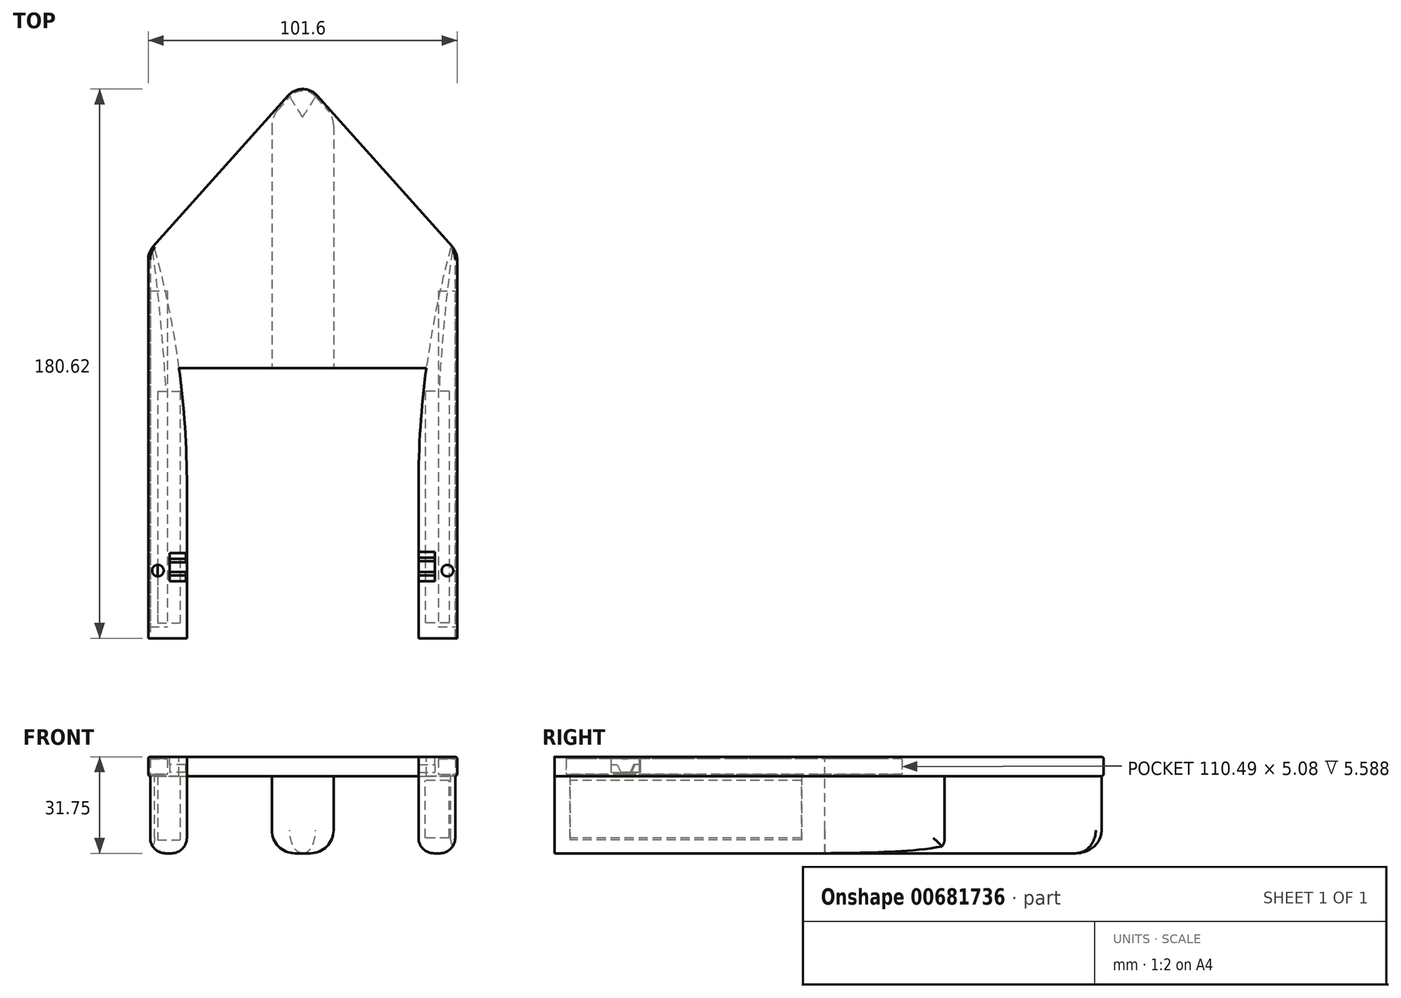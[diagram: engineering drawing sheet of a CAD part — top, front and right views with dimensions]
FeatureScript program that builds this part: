
annotation { "Feature Type Name" : "Feature", "Feature Type Description" : "" }
export const myFeature = defineFeature(function(context is Context, id is Id, definition is map)
    precondition{}
    {
        {
            var Q0;
            Q0=qCreatedBy(makeId("Top.planeOp"),FACE);
            var sketch = newSketch(context, id + "F0", { "sketchPlane" : qUnion([Q0])});
            skLineSegment(sketch, "E0", {"start": v(-75.35, 48.14) * mm, "end": v(-75.35, -78.86) * mm});
            skLineSegment(sketch, "E1", {"start": v(-75.35, -78.86) * mm, "end": v(26.25, -78.86) * mm});
            skLineSegment(sketch, "E2", {"start": v(26.25, -78.86) * mm, "end": v(26.25, 48.14) * mm});
            skLineSegment(sketch, "E3", {"start": v(-75.35, 48.14) * mm, "end": v(-24.55, 104.93) * mm});
            skLineSegment(sketch, "E4", {"start": v(-24.55, 104.93) * mm, "end": v(26.25, 48.14) * mm});
            skSolve(sketch);
        }
        {
            var Q0;
            Q0 = qSketchRegion(id + "F0", true);
            extrude(context, id + "F1", {"entities" : qUnion([Q0]), "depth" : 6.35 * mm, "offsetDistance" : 25.4 * mm});
        }
        {
            var Q0;
            Q0=makeQuery(id+"F1.opExtrude","SWEPT_EDGE",EDGE,{"disambiguationData":[OSD([sQuery(id+"F0.wireOp",EDGE,"E3"),sQuery(id+"F0.wireOp",EDGE,"E4")])]});
            var Q1;
            Q1=makeQuery(id+"F1.opExtrude","SWEPT_EDGE",EDGE,{"disambiguationData":[OSD([sQuery(id+"F0.wireOp",EDGE,"E0"),sQuery(id+"F0.wireOp",EDGE,"E3")])]});
            var Q2;
            Q2=makeQuery(id+"F1.opExtrude","SWEPT_EDGE",EDGE,{"disambiguationData":[OSD([sQuery(id+"F0.wireOp",EDGE,"E2"),sQuery(id+"F0.wireOp",EDGE,"E4")])]});
            fillet(context, id + "F2", {"entities" : qUnion([Q0, Q1, Q2]), "radius" : 6.35 * mm, "tangentPropagation" : true, "allowEdgeOverflow" : false});
        }
        {
            var Q0;
            Q0=makeQuery(id+"F1.opExtrude","CAP_EDGE",EDGE,{"disambiguationData":[OSD([sQuery(id+"F0.wireOp",EDGE,"E3")])],"isStart":false});
            var Q1;
            Q1=makeQuery(id+"F1.opExtrude","CAP_EDGE",EDGE,{"disambiguationData":[OSD([sQuery(id+"F0.wireOp",EDGE,"E4")])],"isStart":true});
            var Q2;
            Q2=makeQuery(id+"F1.opExtrude","CAP_EDGE",EDGE,{"disambiguationData":[OSD([sQuery(id+"F0.wireOp",EDGE,"E3")])],"isStart":true});
            var Q3;
            {var subQ0=sQuery(id+"F0.wireOp",EDGE,"E4");var subQ1=sQuery(id+"F0.wireOp",EDGE,"E3");Q3=makeQuery(id+"F2.opFillet","BLEND_EDGE",EDGE,{"blendedFrom":[makeQuery(id+"F1.opExtrude","SWEPT_EDGE",EDGE,{"disambiguationData":[OSD([subQ1,subQ0])]}),makeQuery(id+"F1.opExtrude","CAP_FACE",FACE,{"disambiguationData":[OSD([sQuery(id+"F0.wireOp",EDGE,"E0"),sQuery(id+"F0.wireOp",EDGE,"E1"),sQuery(id+"F0.wireOp",EDGE,"E2"),subQ1,subQ0])],"isStart":true})],"blendedInto":[makeQuery(id+"F1.opExtrude","CAP_FACE",FACE,{"disambiguationData":[OSD([sQuery(id+"F0.wireOp",EDGE,"E0"),sQuery(id+"F0.wireOp",EDGE,"E1"),sQuery(id+"F0.wireOp",EDGE,"E2"),subQ1,subQ0])],"isStart":true})]});}
            fillet(context, id + "F3", {"entities" : qUnion([Q0, Q1, Q2, Q3]), "radius" : 0.64 * mm, "tangentPropagation" : true, "allowEdgeOverflow" : false});
        }
        {
            var Q0;
            Q0=makeQuery(id+"F1.opExtrude","CAP_FACE",FACE,{"disambiguationData":[OSD([sQuery(id+"F0.wireOp",EDGE,"E0"),sQuery(id+"F0.wireOp",EDGE,"E1"),sQuery(id+"F0.wireOp",EDGE,"E2"),sQuery(id+"F0.wireOp",EDGE,"E3"),sQuery(id+"F0.wireOp",EDGE,"E4")])],"isStart":false});
            var sketch = newSketch(context, id + "F4", { "sketchPlane" : qUnion([Q0])});
            skLineSegment(sketch, "E5.bottom", {"start": v(-62.65, -78.86) * mm, "end": v(13.55, -78.86) * mm});
            skLineSegment(sketch, "E5.top", {"start": v(-62.65, 10.04) * mm, "end": v(13.55, 10.04) * mm});
            skLineSegment(sketch, "E5.left", {"start": v(-62.65, -78.86) * mm, "end": v(-62.65, 10.04) * mm});
            skLineSegment(sketch, "E5.right", {"start": v(13.55, -78.86) * mm, "end": v(13.55, 10.04) * mm});
            skSolve(sketch);
        }
        {
            var Q0;
            Q0 = qSketchRegion(id + "F4", true);
            extrude(context, id + "F5", {"entities" : qUnion([Q0]), "operationType" : NewBodyOperationType.REMOVE, "oppositeDirection" : true, "depth" : 25.4 * mm, "offsetDistance" : 25.4 * mm});
        }
        {
            var Q0;
            Q0=makeQuery(id+"F1.opExtrude","CAP_FACE",FACE,{"disambiguationData":[OSD([sQuery(id+"F0.wireOp",EDGE,"E0"),sQuery(id+"F0.wireOp",EDGE,"E1"),sQuery(id+"F0.wireOp",EDGE,"E2"),sQuery(id+"F0.wireOp",EDGE,"E3"),sQuery(id+"F0.wireOp",EDGE,"E4")])],"isStart":false});
            var sketch = newSketch(context, id + "F6", { "sketchPlane" : qUnion([Q0])});
            skLineSegment(sketch, "E6.bottom", {"start": v(-62.65, -60.09) * mm, "end": v(-68.37, -60.09) * mm});
            skLineSegment(sketch, "E6.top", {"start": v(-62.65, -50.86) * mm, "end": v(-68.37, -50.86) * mm});
            skLineSegment(sketch, "E6.left", {"start": v(-62.65, -60.09) * mm, "end": v(-62.65, -50.86) * mm});
            skLineSegment(sketch, "E6.right", {"start": v(-68.37, -60.09) * mm, "end": v(-68.37, -50.86) * mm});
            skSolve(sketch);
        }
        {
            var Q0;
            Q0 = qSketchRegion(id + "F6", true);
            extrude(context, id + "F7", {"entities" : qUnion([Q0]), "operationType" : NewBodyOperationType.REMOVE, "oppositeDirection" : true, "depth" : 5.08 * mm, "offsetDistance" : 25.4 * mm});
        }
        {
            var Q0;
            Q0=makeQuery(id+"F1.opExtrude","CAP_FACE",FACE,{"disambiguationData":[OSD([sQuery(id+"F0.wireOp",EDGE,"E0"),sQuery(id+"F0.wireOp",EDGE,"E1"),sQuery(id+"F0.wireOp",EDGE,"E2"),sQuery(id+"F0.wireOp",EDGE,"E3"),sQuery(id+"F0.wireOp",EDGE,"E4")])],"isStart":false});
            var sketch = newSketch(context, id + "F8", { "sketchPlane" : qUnion([Q0])});
            skLineSegment(sketch, "E7.bottom", {"start": v(13.55, -50.5) * mm, "end": v(18.92, -50.5) * mm});
            skLineSegment(sketch, "E7.top", {"start": v(13.55, -60.09) * mm, "end": v(18.92, -60.09) * mm});
            skLineSegment(sketch, "E7.left", {"start": v(13.55, -50.5) * mm, "end": v(13.55, -60.09) * mm});
            skLineSegment(sketch, "E7.right", {"start": v(18.92, -50.5) * mm, "end": v(18.92, -60.09) * mm});
            skSolve(sketch);
        }
        {
            var Q0;
            Q0 = qSketchRegion(id + "F8", true);
            extrude(context, id + "F9", {"entities" : qUnion([Q0]), "operationType" : NewBodyOperationType.REMOVE, "oppositeDirection" : true, "depth" : 5.08 * mm, "offsetDistance" : 25.4 * mm});
        }
        {
            var Q0;
            Q0=makeQuery(id+"F7.boolean.opBoolean","COPY",FACE,{"derivedFrom":makeQuery(id+"F7.opExtrude","SWEPT_FACE",FACE,{"disambiguationData":[OSD([sQuery(id+"F6.wireOp",EDGE,"E6.right")])]})});
            var sketch = newSketch(context, id + "F10", { "sketchPlane" : qUnion([Q0])});
            skLineSegment(sketch, "E8", {"start": v(-60.09, 3.81) * mm, "end": v(-58.18, 3.81) * mm});
            skLineSegment(sketch, "E9", {"start": v(-58.18, 3.81) * mm, "end": v(-57.02, 1.27) * mm});
            skLineSegment(sketch, "E10", {"start": v(-57.02, 1.27) * mm, "end": v(-60.09, 1.27) * mm});
            skLineSegment(sketch, "E11", {"start": v(-60.09, 1.27) * mm, "end": v(-60.09, 3.81) * mm});
            skLineSegment(sketch, "E12", {"start": v(-50.86, 3.81) * mm, "end": v(-52.76, 3.81) * mm});
            skLineSegment(sketch, "E13", {"start": v(-52.76, 3.8) * mm, "end": v(-53.93, 1.27) * mm});
            skLineSegment(sketch, "E14", {"start": v(-53.93, 1.27) * mm, "end": v(-50.86, 1.27) * mm});
            skLineSegment(sketch, "E15", {"start": v(-50.86, 1.27) * mm, "end": v(-50.86, 3.81) * mm});
            skSolve(sketch);
        }
        {
            var Q0;
            Q0=makeQuery(id+"F9.boolean.opBoolean","COPY",FACE,{"derivedFrom":makeQuery(id+"F9.opExtrude","SWEPT_FACE",FACE,{"disambiguationData":[OSD([sQuery(id+"F8.wireOp",EDGE,"E7.right")])]})});
            var sketch = newSketch(context, id + "F11", { "sketchPlane" : qUnion([Q0])});
            skLineSegment(sketch, "E16", {"start": v(50.5, 3.81) * mm, "end": v(52.4, 3.81) * mm});
            skLineSegment(sketch, "E17", {"start": v(52.4, 3.81) * mm, "end": v(53.56, 1.27) * mm});
            skLineSegment(sketch, "E18", {"start": v(53.56, 1.27) * mm, "end": v(50.5, 1.27) * mm});
            skLineSegment(sketch, "E19", {"start": v(50.5, 1.27) * mm, "end": v(50.5, 3.81) * mm});
            skLineSegment(sketch, "E20", {"start": v(60.09, 3.81) * mm, "end": v(58.18, 3.81) * mm});
            skLineSegment(sketch, "E21", {"start": v(58.18, 3.81) * mm, "end": v(57.02, 1.27) * mm});
            skLineSegment(sketch, "E22", {"start": v(57.02, 1.27) * mm, "end": v(60.09, 1.27) * mm});
            skLineSegment(sketch, "E23", {"start": v(60.09, 1.27) * mm, "end": v(60.09, 3.81) * mm});
            skSolve(sketch);
        }
        {
            var Q0;
            Q0 = qSketchRegion(id + "F10", true);
            extrude(context, id + "F12", {"entities" : qUnion([Q0]), "operationType" : NewBodyOperationType.ADD, "depth" : 5.33 * mm, "offsetDistance" : 25.4 * mm});
        }
        {
            var Q0;
            Q0 = qSketchRegion(id + "F11", true);
            extrude(context, id + "F13", {"entities" : qUnion([Q0]), "operationType" : NewBodyOperationType.ADD, "depth" : 5.33 * mm, "offsetDistance" : 25.4 * mm});
        }
        {
            var Q0;
            {var subQ0=sQuery(id+"FkVk3INAum2beZh_1.wireOp",EDGE,"CBnXaj17-lKBn-qkcq-8vhT-qGtuAPUyLBLH.right");var subQ1=sQuery(id+"FkVk3INAum2beZh_1.wireOp",EDGE,"CBnXaj17-lKBn-qkcq-8vhT-qGtuAPUyLBLH.top");var subQ2=sQuery(id+"FkVk3INAum2beZh_1.wireOp",EDGE,"CBnXaj17-lKBn-qkcq-8vhT-qGtuAPUyLBLH.left");var subQ3=sQuery(id+"F0.wireOp",EDGE,"E0");var subQ7=sQuery(id+"F0.wireOp",EDGE,"E1");Q0=makeQuery(id+"F5p0aCiFBfXdLHS_1.boolean.opBoolean","MERGE",FACE,{"derivedFrom":[makeQuery(id+"F5.boolean.opBoolean","SPLIT",FACE,{"disambiguationData":[TD([makeQuery(id+"F1.opExtrude","SWEPT_FACE",FACE,{"disambiguationData":[OSD([subQ3])]})])],"derivedFrom":makeQuery(id+"FswQXXDHsv7HpHE_1.boolean.opBoolean","MERGE",FACE,{"derivedFrom":[makeQuery(id+"F1.opExtrude","SWEPT_FACE",FACE,{"disambiguationData":[OSD([subQ7])]}),makeQuery(id+"FswQXXDHsv7HpHE_1.opExtrude","CAP_FACE",FACE,{"disambiguationData":[OSD([sQuery(id+"FkVk3INAum2beZh_1.wireOp",EDGE,"CBnXaj17-lKBn-qkcq-8vhT-qGtuAPUyLBLH.bottom"),subQ1,subQ2,subQ0])],"isStart":true}),makeQuery(id+"FswQXXDHsv7HpHE_1.opExtrude","CAP_FACE",FACE,{"disambiguationData":[OSD([sQuery(id+"FkVk3INAum2beZh_1.wireOp",EDGE,"G5rZIyKY-4YGs-gmH6-VOyw-JunLJIaNOIT2.bottom"),sQuery(id+"FkVk3INAum2beZh_1.wireOp",EDGE,"G5rZIyKY-4YGs-gmH6-VOyw-JunLJIaNOIT2.top"),sQuery(id+"FkVk3INAum2beZh_1.wireOp",EDGE,"G5rZIyKY-4YGs-gmH6-VOyw-JunLJIaNOIT2.left"),sQuery(id+"FkVk3INAum2beZh_1.wireOp",EDGE,"G5rZIyKY-4YGs-gmH6-VOyw-JunLJIaNOIT2.right")])],"isStart":true})]})}),makeQuery(id+"F5p0aCiFBfXdLHS_1.opExtrude","CAP_FACE",FACE,{"disambiguationData":[OSD([sQuery(id+"FsEtyhvZ73HZmaM_1.wireOp",EDGE,"eh50Zago-m3CJ-1YUL-9TTU-CO1hKXEADzyN.bottom"),sQuery(id+"FsEtyhvZ73HZmaM_1.wireOp",EDGE,"eh50Zago-m3CJ-1YUL-9TTU-CO1hKXEADzyN.top"),sQuery(id+"FsEtyhvZ73HZmaM_1.wireOp",EDGE,"eh50Zago-m3CJ-1YUL-9TTU-CO1hKXEADzyN.left"),sQuery(id+"FsEtyhvZ73HZmaM_1.wireOp",EDGE,"eh50Zago-m3CJ-1YUL-9TTU-CO1hKXEADzyN.right")])],"isStart":true})]});}
            var sketch = newSketch(context, id + "F14", { "sketchPlane" : qUnion([Q0])});
            skLineSegment(sketch, "E24.bottom", {"start": v(-74.72, 5.72) * mm, "end": v(-69.13, 5.72) * mm});
            skLineSegment(sketch, "E24.top", {"start": v(-74.72, 0.63) * mm, "end": v(-69.13, 0.63) * mm});
            skLineSegment(sketch, "E24.left", {"start": v(-74.72, 5.72) * mm, "end": v(-74.72, 0.63) * mm});
            skLineSegment(sketch, "E24.right", {"start": v(-69.13, 5.72) * mm, "end": v(-69.13, 0.63) * mm});
            skSolve(sketch);
        }
        {
            var Q0;
            {var subQ0=sQuery(id+"FkVk3INAum2beZh_1.wireOp",EDGE,"G5rZIyKY-4YGs-gmH6-VOyw-JunLJIaNOIT2.right");var subQ1=sQuery(id+"FkVk3INAum2beZh_1.wireOp",EDGE,"G5rZIyKY-4YGs-gmH6-VOyw-JunLJIaNOIT2.top");var subQ2=sQuery(id+"F0.wireOp",EDGE,"E2");var subQ3=sQuery(id+"FkVk3INAum2beZh_1.wireOp",EDGE,"G5rZIyKY-4YGs-gmH6-VOyw-JunLJIaNOIT2.left");var subQ6=sQuery(id+"F0.wireOp",EDGE,"E1");Q0=makeQuery(id+"FzT6SfWKQMYkcEQ_1.boolean.opBoolean","MERGE",FACE,{"derivedFrom":[makeQuery(id+"F5.boolean.opBoolean","SPLIT",FACE,{"disambiguationData":[TD([makeQuery(id+"F1.opExtrude","SWEPT_FACE",FACE,{"disambiguationData":[OSD([subQ2])]})])],"derivedFrom":makeQuery(id+"FswQXXDHsv7HpHE_1.boolean.opBoolean","MERGE",FACE,{"derivedFrom":[makeQuery(id+"F1.opExtrude","SWEPT_FACE",FACE,{"disambiguationData":[OSD([subQ6])]}),makeQuery(id+"FswQXXDHsv7HpHE_1.opExtrude","CAP_FACE",FACE,{"disambiguationData":[OSD([sQuery(id+"FkVk3INAum2beZh_1.wireOp",EDGE,"CBnXaj17-lKBn-qkcq-8vhT-qGtuAPUyLBLH.bottom"),sQuery(id+"FkVk3INAum2beZh_1.wireOp",EDGE,"CBnXaj17-lKBn-qkcq-8vhT-qGtuAPUyLBLH.top"),sQuery(id+"FkVk3INAum2beZh_1.wireOp",EDGE,"CBnXaj17-lKBn-qkcq-8vhT-qGtuAPUyLBLH.left"),sQuery(id+"FkVk3INAum2beZh_1.wireOp",EDGE,"CBnXaj17-lKBn-qkcq-8vhT-qGtuAPUyLBLH.right")])],"isStart":true}),makeQuery(id+"FswQXXDHsv7HpHE_1.opExtrude","CAP_FACE",FACE,{"disambiguationData":[OSD([sQuery(id+"FkVk3INAum2beZh_1.wireOp",EDGE,"G5rZIyKY-4YGs-gmH6-VOyw-JunLJIaNOIT2.bottom"),subQ1,subQ3,subQ0])],"isStart":true})]})}),makeQuery(id+"FzT6SfWKQMYkcEQ_1.opExtrude","CAP_FACE",FACE,{"disambiguationData":[OSD([sQuery(id+"F95VfNdrVZvIhjE_1.wireOp",EDGE,"nyIf93XB-J9r0-geGF-N8j9-ZKfysJtzp2Ce.bottom"),sQuery(id+"F95VfNdrVZvIhjE_1.wireOp",EDGE,"nyIf93XB-J9r0-geGF-N8j9-ZKfysJtzp2Ce.top"),sQuery(id+"F95VfNdrVZvIhjE_1.wireOp",EDGE,"nyIf93XB-J9r0-geGF-N8j9-ZKfysJtzp2Ce.left"),sQuery(id+"F95VfNdrVZvIhjE_1.wireOp",EDGE,"nyIf93XB-J9r0-geGF-N8j9-ZKfysJtzp2Ce.right")])],"isStart":true})]});}
            var sketch = newSketch(context, id + "F15", { "sketchPlane" : qUnion([Q0])});
            skLineSegment(sketch, "E25.bottom", {"start": v(20.02, 5.72) * mm, "end": v(25.61, 5.72) * mm});
            skLineSegment(sketch, "E25.top", {"start": v(20.02, 0.64) * mm, "end": v(25.61, 0.64) * mm});
            skLineSegment(sketch, "E25.left", {"start": v(20.02, 5.72) * mm, "end": v(20.02, 0.64) * mm});
            skLineSegment(sketch, "E25.right", {"start": v(25.61, 5.72) * mm, "end": v(25.61, 0.64) * mm});
            skSolve(sketch);
        }
        {
            var Q0;
            Q0 = qSketchRegion(id + "F14", true);
            extrude(context, id + "F16", {"entities" : qUnion([Q0]), "operationType" : NewBodyOperationType.REMOVE, "oppositeDirection" : true, "depth" : 114.3 * mm, "offsetDistance" : 25.4 * mm});
        }
        {
            var Q0;
            Q0 = qSketchRegion(id + "F15", true);
            extrude(context, id + "F17", {"entities" : qUnion([Q0]), "operationType" : NewBodyOperationType.REMOVE, "oppositeDirection" : true, "depth" : 114.3 * mm, "offsetDistance" : 25.4 * mm});
        }
        {
            var Q0;
            {var subQ0=sQuery(id+"FkVk3INAum2beZh_1.wireOp",EDGE,"G5rZIyKY-4YGs-gmH6-VOyw-JunLJIaNOIT2.right");var subQ1=sQuery(id+"FkVk3INAum2beZh_1.wireOp",EDGE,"G5rZIyKY-4YGs-gmH6-VOyw-JunLJIaNOIT2.top");var subQ2=sQuery(id+"F0.wireOp",EDGE,"E2");var subQ3=sQuery(id+"FkVk3INAum2beZh_1.wireOp",EDGE,"G5rZIyKY-4YGs-gmH6-VOyw-JunLJIaNOIT2.left");var subQ6=sQuery(id+"F0.wireOp",EDGE,"E1");Q0=makeQuery(id+"FzT6SfWKQMYkcEQ_1.boolean.opBoolean","MERGE",FACE,{"derivedFrom":[makeQuery(id+"F5.boolean.opBoolean","SPLIT",FACE,{"disambiguationData":[TD([makeQuery(id+"F1.opExtrude","SWEPT_FACE",FACE,{"disambiguationData":[OSD([subQ2])]})])],"derivedFrom":makeQuery(id+"FswQXXDHsv7HpHE_1.boolean.opBoolean","MERGE",FACE,{"derivedFrom":[makeQuery(id+"F1.opExtrude","SWEPT_FACE",FACE,{"disambiguationData":[OSD([subQ6])]}),makeQuery(id+"FswQXXDHsv7HpHE_1.opExtrude","CAP_FACE",FACE,{"disambiguationData":[OSD([sQuery(id+"FkVk3INAum2beZh_1.wireOp",EDGE,"CBnXaj17-lKBn-qkcq-8vhT-qGtuAPUyLBLH.bottom"),sQuery(id+"FkVk3INAum2beZh_1.wireOp",EDGE,"CBnXaj17-lKBn-qkcq-8vhT-qGtuAPUyLBLH.top"),sQuery(id+"FkVk3INAum2beZh_1.wireOp",EDGE,"CBnXaj17-lKBn-qkcq-8vhT-qGtuAPUyLBLH.left"),sQuery(id+"FkVk3INAum2beZh_1.wireOp",EDGE,"CBnXaj17-lKBn-qkcq-8vhT-qGtuAPUyLBLH.right")])],"isStart":true}),makeQuery(id+"FswQXXDHsv7HpHE_1.opExtrude","CAP_FACE",FACE,{"disambiguationData":[OSD([sQuery(id+"FkVk3INAum2beZh_1.wireOp",EDGE,"G5rZIyKY-4YGs-gmH6-VOyw-JunLJIaNOIT2.bottom"),subQ1,subQ3,subQ0])],"isStart":true})]})}),makeQuery(id+"FzT6SfWKQMYkcEQ_1.opExtrude","CAP_FACE",FACE,{"disambiguationData":[OSD([sQuery(id+"F95VfNdrVZvIhjE_1.wireOp",EDGE,"nyIf93XB-J9r0-geGF-N8j9-ZKfysJtzp2Ce.bottom"),sQuery(id+"F95VfNdrVZvIhjE_1.wireOp",EDGE,"nyIf93XB-J9r0-geGF-N8j9-ZKfysJtzp2Ce.top"),sQuery(id+"F95VfNdrVZvIhjE_1.wireOp",EDGE,"nyIf93XB-J9r0-geGF-N8j9-ZKfysJtzp2Ce.left"),sQuery(id+"F95VfNdrVZvIhjE_1.wireOp",EDGE,"nyIf93XB-J9r0-geGF-N8j9-ZKfysJtzp2Ce.right")])],"isStart":true})]});}
            var sketch = newSketch(context, id + "F18", { "sketchPlane" : qUnion([Q0])});
            skLineSegment(sketch, "E26.bottom", {"start": v(20.02, 5.72) * mm, "end": v(25.61, 5.72) * mm});
            skLineSegment(sketch, "E26.top", {"start": v(20.02, 0.64) * mm, "end": v(25.61, 0.64) * mm});
            skLineSegment(sketch, "E26.left", {"start": v(20.02, 5.72) * mm, "end": v(20.02, 0.64) * mm});
            skLineSegment(sketch, "E26.right", {"start": v(25.61, 5.72) * mm, "end": v(25.61, 0.64) * mm});
            skSolve(sketch);
        }
        {
            var Q0;
            Q0 = qSketchRegion(id + "F18", true);
            extrude(context, id + "F19", {"entities" : qUnion([Q0]), "operationType" : NewBodyOperationType.ADD, "oppositeDirection" : true, "depth" : 3.8 * mm, "offsetDistance" : 25.4 * mm});
        }
        {
            var Q0;
            {var subQ0=sQuery(id+"FkVk3INAum2beZh_1.wireOp",EDGE,"CBnXaj17-lKBn-qkcq-8vhT-qGtuAPUyLBLH.right");var subQ1=sQuery(id+"FkVk3INAum2beZh_1.wireOp",EDGE,"CBnXaj17-lKBn-qkcq-8vhT-qGtuAPUyLBLH.top");var subQ2=sQuery(id+"FkVk3INAum2beZh_1.wireOp",EDGE,"CBnXaj17-lKBn-qkcq-8vhT-qGtuAPUyLBLH.left");var subQ3=sQuery(id+"F0.wireOp",EDGE,"E0");var subQ7=sQuery(id+"F0.wireOp",EDGE,"E1");Q0=makeQuery(id+"F5p0aCiFBfXdLHS_1.boolean.opBoolean","MERGE",FACE,{"derivedFrom":[makeQuery(id+"F5.boolean.opBoolean","SPLIT",FACE,{"disambiguationData":[TD([makeQuery(id+"F1.opExtrude","SWEPT_FACE",FACE,{"disambiguationData":[OSD([subQ3])]})])],"derivedFrom":makeQuery(id+"FswQXXDHsv7HpHE_1.boolean.opBoolean","MERGE",FACE,{"derivedFrom":[makeQuery(id+"F1.opExtrude","SWEPT_FACE",FACE,{"disambiguationData":[OSD([subQ7])]}),makeQuery(id+"FswQXXDHsv7HpHE_1.opExtrude","CAP_FACE",FACE,{"disambiguationData":[OSD([sQuery(id+"FkVk3INAum2beZh_1.wireOp",EDGE,"CBnXaj17-lKBn-qkcq-8vhT-qGtuAPUyLBLH.bottom"),subQ1,subQ2,subQ0])],"isStart":true}),makeQuery(id+"FswQXXDHsv7HpHE_1.opExtrude","CAP_FACE",FACE,{"disambiguationData":[OSD([sQuery(id+"FkVk3INAum2beZh_1.wireOp",EDGE,"G5rZIyKY-4YGs-gmH6-VOyw-JunLJIaNOIT2.bottom"),sQuery(id+"FkVk3INAum2beZh_1.wireOp",EDGE,"G5rZIyKY-4YGs-gmH6-VOyw-JunLJIaNOIT2.top"),sQuery(id+"FkVk3INAum2beZh_1.wireOp",EDGE,"G5rZIyKY-4YGs-gmH6-VOyw-JunLJIaNOIT2.left"),sQuery(id+"FkVk3INAum2beZh_1.wireOp",EDGE,"G5rZIyKY-4YGs-gmH6-VOyw-JunLJIaNOIT2.right")])],"isStart":true})]})}),makeQuery(id+"F5p0aCiFBfXdLHS_1.opExtrude","CAP_FACE",FACE,{"disambiguationData":[OSD([sQuery(id+"FsEtyhvZ73HZmaM_1.wireOp",EDGE,"eh50Zago-m3CJ-1YUL-9TTU-CO1hKXEADzyN.bottom"),sQuery(id+"FsEtyhvZ73HZmaM_1.wireOp",EDGE,"eh50Zago-m3CJ-1YUL-9TTU-CO1hKXEADzyN.top"),sQuery(id+"FsEtyhvZ73HZmaM_1.wireOp",EDGE,"eh50Zago-m3CJ-1YUL-9TTU-CO1hKXEADzyN.left"),sQuery(id+"FsEtyhvZ73HZmaM_1.wireOp",EDGE,"eh50Zago-m3CJ-1YUL-9TTU-CO1hKXEADzyN.right")])],"isStart":true})]});}
            var sketch = newSketch(context, id + "F20", { "sketchPlane" : qUnion([Q0])});
            skLineSegment(sketch, "E27.bottom", {"start": v(-74.72, 5.72) * mm, "end": v(-69.13, 5.72) * mm});
            skLineSegment(sketch, "E27.top", {"start": v(-74.72, 0.63) * mm, "end": v(-69.13, 0.63) * mm});
            skLineSegment(sketch, "E27.left", {"start": v(-74.72, 5.72) * mm, "end": v(-74.72, 0.63) * mm});
            skLineSegment(sketch, "E27.right", {"start": v(-69.13, 5.72) * mm, "end": v(-69.13, 0.63) * mm});
            skSolve(sketch);
        }
        {
            var Q0;
            Q0 = qSketchRegion(id + "F20", true);
            extrude(context, id + "F21", {"entities" : qUnion([Q0]), "operationType" : NewBodyOperationType.ADD, "oppositeDirection" : true, "depth" : 3.8 * mm, "offsetDistance" : 25.4 * mm});
        }
        {
            var Q0;
            Q0=makeQuery(id+"F1.opExtrude","CAP_FACE",FACE,{"disambiguationData":[OSD([sQuery(id+"F0.wireOp",EDGE,"E0"),sQuery(id+"F0.wireOp",EDGE,"E1"),sQuery(id+"F0.wireOp",EDGE,"E2"),sQuery(id+"F0.wireOp",EDGE,"E3"),sQuery(id+"F0.wireOp",EDGE,"E4")])],"isStart":false});
            var sketch = newSketch(context, id + "F22", { "sketchPlane" : qUnion([Q0])});
            skCircle(sketch, "E28", {"center": v(-72.18, -56.64) * mm, "radius": 1.9 * mm});
            skCircle(sketch, "E29", {"center": v(23.07, -56.64) * mm, "radius": 1.9 * mm});
            skSolve(sketch);
        }
        {
            var Q0;
            Q0 = qSketchRegion(id + "F22", true);
            extrude(context, id + "F23", {"entities" : qUnion([Q0]), "operationType" : NewBodyOperationType.REMOVE, "oppositeDirection" : true, "depth" : 12.7 * mm, "offsetDistance" : 25.4 * mm});
        }
        {
            var Q0;
            Q0=makeQuery(id+"F1.opExtrude","CAP_FACE",FACE,{"disambiguationData":[OSD([sQuery(id+"F0.wireOp",EDGE,"E0"),sQuery(id+"F0.wireOp",EDGE,"E1"),sQuery(id+"F0.wireOp",EDGE,"E2"),sQuery(id+"F0.wireOp",EDGE,"E3"),sQuery(id+"F0.wireOp",EDGE,"E4")])],"isStart":true});
            var sketch = newSketch(context, id + "F24", { "sketchPlane" : qUnion([Q0])});
            skLineSegment(sketch, "E30.bottom", {"start": v(25.61, -45.7) * mm, "end": v(13.55, -45.7) * mm});
            skLineSegment(sketch, "E30.top", {"start": v(25.61, 78.86) * mm, "end": v(13.55, 78.86) * mm});
            skLineSegment(sketch, "E30.left", {"start": v(25.61, -45.7) * mm, "end": v(25.61, 78.86) * mm});
            skLineSegment(sketch, "E30.right", {"start": v(13.55, -45.7) * mm, "end": v(13.55, 78.86) * mm});
            skLineSegment(sketch, "E31", {"start": v(13.55, -45.7) * mm, "end": v(13.55, -61.38) * mm});
            skArc(sketch, "E32", {"start": v(24.15, -49.52) * mm, "mid": v(25.23, -47.75) * mm, "end": v(25.61, -45.7) * mm});
            skLineSegment(sketch, "E33", {"start": v(24.15, -49.52) * mm, "end": v(13.55, -61.38) * mm});
            skSolve(sketch);
        }
        {
            var Q0;
            Q0 = qSketchRegion(id + "F24", true);
            extrude(context, id + "F25", {"entities" : qUnion([Q0]), "operationType" : NewBodyOperationType.ADD, "depth" : 25.4 * mm, "offsetDistance" : 25.4 * mm});
        }
        {
            var Q0;
            Q0=makeQuery(id+"F1.opExtrude","CAP_FACE",FACE,{"disambiguationData":[OSD([sQuery(id+"F0.wireOp",EDGE,"E0"),sQuery(id+"F0.wireOp",EDGE,"E1"),sQuery(id+"F0.wireOp",EDGE,"E2"),sQuery(id+"F0.wireOp",EDGE,"E3"),sQuery(id+"F0.wireOp",EDGE,"E4")])],"isStart":true});
            var sketch = newSketch(context, id + "F26", { "sketchPlane" : qUnion([Q0])});
            skLineSegment(sketch, "E34.bottom", {"start": v(-14.4, -92.62) * mm, "end": v(-34.71, -92.62) * mm});
            skLineSegment(sketch, "E34.top", {"start": v(-14.4, -10.07) * mm, "end": v(-34.71, -10.07) * mm});
            skLineSegment(sketch, "E34.left", {"start": v(-14.4, -92.62) * mm, "end": v(-14.4, -10.07) * mm});
            skLineSegment(sketch, "E34.right", {"start": v(-34.71, -92.62) * mm, "end": v(-34.71, -10.07) * mm});
            skLineSegment(sketch, "E35", {"start": v(-14.4, -92.62) * mm, "end": v(-20.3, -99.22) * mm});
            skLineSegment(sketch, "E36", {"start": v(-34.71, -92.62) * mm, "end": v(-28.81, -99.22) * mm});
            skArc(sketch, "E37", {"start": v(-28.81, -99.22) * mm, "mid": v(-24.55, -101.12) * mm, "end": v(-20.3, -99.22) * mm});
            skSolve(sketch);
        }
        {
            var Q0;
            Q0 = qSketchRegion(id + "F26", true);
            extrude(context, id + "F27", {"entities" : qUnion([Q0]), "operationType" : NewBodyOperationType.ADD, "depth" : 25.4 * mm, "offsetDistance" : 25.4 * mm});
        }
        {
            var Q0;
            Q0=makeQuery(id+"F25.opExtrude","SWEPT_EDGE",EDGE,{"disambiguationData":[OSD([sQuery(id+"F0.wireOp",EDGE,"E0"),sQuery(id+"F0.wireOp",EDGE,"E1"),sQuery(id+"F0.wireOp",EDGE,"E2"),sQuery(id+"F0.wireOp",EDGE,"E3"),sQuery(id+"F0.wireOp",EDGE,"E4"),sQuery(id+"F24.wireOp",EDGE,"E31"),sQuery(id+"F24.wireOp",EDGE,"E33")])]});
            fillet(context, id + "F28", {"entities" : qUnion([Q0]), "radius" : 294.8 * mm, "tangentPropagation" : true, "allowEdgeOverflow" : false});
        }
        {
            var Q0;
            Q0=makeQuery(id+"F27.opExtrude","CAP_EDGE",EDGE,{"disambiguationData":[OSD([sQuery(id+"F26.wireOp",EDGE,"E34.left")])],"isStart":false});
            var Q1;
            Q1=makeQuery(id+"F27.opExtrude","CAP_EDGE",EDGE,{"disambiguationData":[OSD([sQuery(id+"F26.wireOp",EDGE,"E34.right")])],"isStart":false});
            var Q2;
            Q2=makeQuery(id+"F27.opExtrude","SWEPT_EDGE",EDGE,{"disambiguationData":[OSD([sQuery(id+"F0.wireOp",EDGE,"E0"),sQuery(id+"F0.wireOp",EDGE,"E1"),sQuery(id+"F0.wireOp",EDGE,"E2"),sQuery(id+"F0.wireOp",EDGE,"E3"),sQuery(id+"F0.wireOp",EDGE,"E4"),sQuery(id+"F26.wireOp",EDGE,"E34.bottom"),sQuery(id+"F26.wireOp",EDGE,"E34.right"),sQuery(id+"F26.wireOp",EDGE,"E36")])]});
            var Q3;
            Q3=makeQuery(id+"F27.opExtrude","SWEPT_EDGE",EDGE,{"disambiguationData":[OSD([sQuery(id+"F0.wireOp",EDGE,"E0"),sQuery(id+"F0.wireOp",EDGE,"E1"),sQuery(id+"F0.wireOp",EDGE,"E2"),sQuery(id+"F0.wireOp",EDGE,"E3"),sQuery(id+"F0.wireOp",EDGE,"E4"),sQuery(id+"F26.wireOp",EDGE,"E34.bottom"),sQuery(id+"F26.wireOp",EDGE,"E34.left"),sQuery(id+"F26.wireOp",EDGE,"E35")])]});
            var Q4;
            Q4=makeQuery(id+"F27.opExtrude","CAP_EDGE",EDGE,{"disambiguationData":[OSD([sQuery(id+"F26.wireOp",EDGE,"E37")])],"isStart":false});
            fillet(context, id + "F29", {"entities" : qUnion([Q0, Q1, Q2, Q3, Q4]), "radius" : 7.62 * mm, "tangentPropagation" : true, "allowEdgeOverflow" : false});
        }
        {
            var Q0;
            {var subQ0=sQuery(id+"F24.wireOp",EDGE,"E33");var subQ1=sQuery(id+"F24.wireOp",EDGE,"E31");Q0=makeQuery(id+"F28.opFillet","BLEND_EDGE",EDGE,{"blendedFrom":[makeQuery(id+"F25.opExtrude","SWEPT_EDGE",EDGE,{"disambiguationData":[OSD([sQuery(id+"F0.wireOp",EDGE,"E0"),sQuery(id+"F0.wireOp",EDGE,"E1"),sQuery(id+"F0.wireOp",EDGE,"E2"),sQuery(id+"F0.wireOp",EDGE,"E3"),sQuery(id+"F0.wireOp",EDGE,"E4"),subQ1,subQ0])]}),makeQuery(id+"F25.opExtrude","CAP_FACE",FACE,{"disambiguationData":[OSD([sQuery(id+"F24.wireOp",EDGE,"E30.top"),sQuery(id+"F24.wireOp",EDGE,"E30.left"),sQuery(id+"F24.wireOp",EDGE,"E30.right"),subQ1,sQuery(id+"F24.wireOp",EDGE,"E32"),subQ0])],"isStart":false})],"blendedInto":[makeQuery(id+"F25.opExtrude","CAP_FACE",FACE,{"disambiguationData":[OSD([sQuery(id+"F24.wireOp",EDGE,"E30.top"),sQuery(id+"F24.wireOp",EDGE,"E30.left"),sQuery(id+"F24.wireOp",EDGE,"E30.right"),subQ1,sQuery(id+"F24.wireOp",EDGE,"E32"),subQ0])],"isStart":false})]});}
            var Q1;
            Q1=makeQuery(id+"F25.opExtrude","CAP_EDGE",EDGE,{"disambiguationData":[OSD([sQuery(id+"F24.wireOp",EDGE,"E30.left")])],"isStart":false});
            fillet(context, id + "F30", {"entities" : qUnion([Q0, Q1]), "radius" : 5.08 * mm, "tangentPropagation" : true, "allowEdgeOverflow" : false});
        }
        {
            var Q0;
            Q0=makeQuery(id+"F1.opExtrude","CAP_FACE",FACE,{"disambiguationData":[OSD([sQuery(id+"F0.wireOp",EDGE,"E0"),sQuery(id+"F0.wireOp",EDGE,"E1"),sQuery(id+"F0.wireOp",EDGE,"E2"),sQuery(id+"F0.wireOp",EDGE,"E3"),sQuery(id+"F0.wireOp",EDGE,"E4")])],"isStart":true});
            var sketch = newSketch(context, id + "F31", { "sketchPlane" : qUnion([Q0])});
            skLineSegment(sketch, "E38.bottom", {"start": v(-74.72, 78.86) * mm, "end": v(-62.65, 78.86) * mm});
            skLineSegment(sketch, "E38.top", {"start": v(-74.72, -45.72) * mm, "end": v(-62.65, -45.72) * mm});
            skLineSegment(sketch, "E38.left", {"start": v(-74.72, 78.86) * mm, "end": v(-74.72, -45.72) * mm});
            skLineSegment(sketch, "E38.right", {"start": v(-62.65, 78.86) * mm, "end": v(-62.65, -45.72) * mm});
            skLineSegment(sketch, "E39", {"start": v(-62.65, -45.72) * mm, "end": v(-62.65, -61.38) * mm});
            skLineSegment(sketch, "E40", {"start": v(-62.65, -61.38) * mm, "end": v(-73.26, -49.52) * mm});
            skArc(sketch, "E41", {"start": v(-74.72, -45.72) * mm, "mid": v(-74.34, -47.75) * mm, "end": v(-73.26, -49.52) * mm});
            skSolve(sketch);
        }
        {
            var Q0;
            Q0 = qSketchRegion(id + "F31", true);
            extrude(context, id + "F32", {"entities" : qUnion([Q0]), "operationType" : NewBodyOperationType.ADD, "depth" : 25.4 * mm, "offsetDistance" : 25.4 * mm});
        }
        {
            var Q0;
            Q0=makeQuery(id+"F32.opExtrude","SWEPT_EDGE",EDGE,{"disambiguationData":[OSD([sQuery(id+"F0.wireOp",EDGE,"E0"),sQuery(id+"F0.wireOp",EDGE,"E1"),sQuery(id+"F0.wireOp",EDGE,"E2"),sQuery(id+"F0.wireOp",EDGE,"E3"),sQuery(id+"F0.wireOp",EDGE,"E4"),sQuery(id+"F31.wireOp",EDGE,"E39"),sQuery(id+"F31.wireOp",EDGE,"E40")])]});
            fillet(context, id + "F33", {"entities" : qUnion([Q0]), "radius" : 294.8 * mm, "tangentPropagation" : true, "allowEdgeOverflow" : false});
        }
        {
            var Q0;
            Q0=makeQuery(id+"F32.opExtrude","CAP_EDGE",EDGE,{"disambiguationData":[OSD([sQuery(id+"F31.wireOp",EDGE,"E38.left")])],"isStart":false});
            var Q1;
            {var subQ0=sQuery(id+"F31.wireOp",EDGE,"E40");var subQ1=sQuery(id+"F31.wireOp",EDGE,"E39");Q1=makeQuery(id+"F33.opFillet","BLEND_EDGE",EDGE,{"blendedFrom":[makeQuery(id+"F32.opExtrude","SWEPT_EDGE",EDGE,{"disambiguationData":[OSD([sQuery(id+"F0.wireOp",EDGE,"E0"),sQuery(id+"F0.wireOp",EDGE,"E1"),sQuery(id+"F0.wireOp",EDGE,"E2"),sQuery(id+"F0.wireOp",EDGE,"E3"),sQuery(id+"F0.wireOp",EDGE,"E4"),subQ1,subQ0])]}),makeQuery(id+"F32.opExtrude","CAP_FACE",FACE,{"disambiguationData":[OSD([sQuery(id+"F31.wireOp",EDGE,"E38.bottom"),sQuery(id+"F31.wireOp",EDGE,"E38.left"),sQuery(id+"F31.wireOp",EDGE,"E38.right"),subQ1,subQ0,sQuery(id+"F31.wireOp",EDGE,"E41")])],"isStart":false})],"blendedInto":[makeQuery(id+"F32.opExtrude","CAP_FACE",FACE,{"disambiguationData":[OSD([sQuery(id+"F31.wireOp",EDGE,"E38.bottom"),sQuery(id+"F31.wireOp",EDGE,"E38.left"),sQuery(id+"F31.wireOp",EDGE,"E38.right"),subQ1,subQ0,sQuery(id+"F31.wireOp",EDGE,"E41")])],"isStart":false})]});}
            fillet(context, id + "F34", {"entities" : qUnion([Q0, Q1]), "radius" : 5.08 * mm, "tangentPropagation" : true, "allowEdgeOverflow" : false});
        }
        {
            var Q0;
            {var subQ0=sQuery(id+"F0.wireOp",EDGE,"E2");var subQ3=sQuery(id+"F0.wireOp",EDGE,"E1");Q0=makeQuery(id+"F25.boolean.opBoolean","MERGE",FACE,{"derivedFrom":[makeQuery(id+"F19.boolean.opBoolean","MERGE",FACE,{"derivedFrom":[makeQuery(id+"F5.boolean.opBoolean","SPLIT",FACE,{"disambiguationData":[TD([makeQuery(id+"F1.opExtrude","SWEPT_FACE",FACE,{"disambiguationData":[OSD([subQ0])]})])],"derivedFrom":makeQuery(id+"F1.opExtrude","SWEPT_FACE",FACE,{"disambiguationData":[OSD([subQ3])]})}),makeQuery(id+"F19.opExtrude","CAP_FACE",FACE,{"disambiguationData":[OSD([sQuery(id+"F18.wireOp",EDGE,"E26.bottom"),sQuery(id+"F18.wireOp",EDGE,"E26.top"),sQuery(id+"F18.wireOp",EDGE,"E26.left"),sQuery(id+"F18.wireOp",EDGE,"E26.right")])],"isStart":true})]}),makeQuery(id+"F25.opExtrude","SWEPT_FACE",FACE,{"disambiguationData":[OSD([sQuery(id+"F24.wireOp",EDGE,"E30.top")])]})]});}
            var sketch = newSketch(context, id + "F35", { "sketchPlane" : qUnion([Q0])});
            skLineSegment(sketch, "E42.left", {"start": v(23.61, -20.32) * mm, "end": v(23.61, -20.32) * mm});
            skLineSegment(sketch, "E43.bottom", {"start": v(23.61, -20.32) * mm, "end": v(15.77, -20.32) * mm});
            skLineSegment(sketch, "E43.top", {"start": v(23.61, -1.5) * mm, "end": v(15.77, -1.5) * mm});
            skLineSegment(sketch, "E43.left", {"start": v(23.61, -20.32) * mm, "end": v(23.61, -1.5) * mm});
            skLineSegment(sketch, "E43.right", {"start": v(15.77, -20.32) * mm, "end": v(15.77, -1.5) * mm});
            skSolve(sketch);
        }
        {
            var Q0;
            Q0 = qSketchRegion(id + "F35", true);
            extrude(context, id + "F36", {"entities" : qUnion([Q0]), "operationType" : NewBodyOperationType.REMOVE, "oppositeDirection" : true, "depth" : 81.28 * mm, "offsetDistance" : 25.4 * mm});
        }
        {
            var Q0;
            {var subQ0=sQuery(id+"F0.wireOp",EDGE,"E0");var subQ4=sQuery(id+"F0.wireOp",EDGE,"E1");Q0=makeQuery(id+"F32.boolean.opBoolean","MERGE",FACE,{"derivedFrom":[makeQuery(id+"F21.boolean.opBoolean","MERGE",FACE,{"derivedFrom":[makeQuery(id+"F5.boolean.opBoolean","SPLIT",FACE,{"disambiguationData":[TD([makeQuery(id+"F1.opExtrude","SWEPT_FACE",FACE,{"disambiguationData":[OSD([subQ0])]})])],"derivedFrom":makeQuery(id+"F1.opExtrude","SWEPT_FACE",FACE,{"disambiguationData":[OSD([subQ4])]})}),makeQuery(id+"F21.opExtrude","CAP_FACE",FACE,{"disambiguationData":[OSD([sQuery(id+"F20.wireOp",EDGE,"E27.bottom"),sQuery(id+"F20.wireOp",EDGE,"E27.top"),sQuery(id+"F20.wireOp",EDGE,"E27.left"),sQuery(id+"F20.wireOp",EDGE,"E27.right")])],"isStart":true})]}),makeQuery(id+"F32.opExtrude","SWEPT_FACE",FACE,{"disambiguationData":[OSD([sQuery(id+"F31.wireOp",EDGE,"E38.bottom")])]})]});}
            var sketch = newSketch(context, id + "F37", { "sketchPlane" : qUnion([Q0])});
            skLineSegment(sketch, "E44.bottom", {"start": v(-72.28, 0) * mm, "end": v(-64.83, 0) * mm});
            skLineSegment(sketch, "E44.top", {"start": v(-72.28, -21.03) * mm, "end": v(-64.83, -21.03) * mm});
            skLineSegment(sketch, "E44.left", {"start": v(-72.28, 0) * mm, "end": v(-72.28, -21.03) * mm});
            skLineSegment(sketch, "E44.right", {"start": v(-64.83, 0) * mm, "end": v(-64.83, -21.03) * mm});
            skSolve(sketch);
        }
        {
            var Q0;
            Q0 = qSketchRegion(id + "F37", true);
            extrude(context, id + "F38", {"entities" : qUnion([Q0]), "operationType" : NewBodyOperationType.REMOVE, "oppositeDirection" : true, "depth" : 81.28 * mm, "offsetDistance" : 25.4 * mm});
        }
        {
            var Q0;
            {var subQ0=sQuery(id+"F0.wireOp",EDGE,"E0");var subQ4=sQuery(id+"F0.wireOp",EDGE,"E1");Q0=makeQuery(id+"F32.boolean.opBoolean","MERGE",FACE,{"derivedFrom":[makeQuery(id+"F21.boolean.opBoolean","MERGE",FACE,{"derivedFrom":[makeQuery(id+"F5.boolean.opBoolean","SPLIT",FACE,{"disambiguationData":[TD([makeQuery(id+"F1.opExtrude","SWEPT_FACE",FACE,{"disambiguationData":[OSD([subQ0])]})])],"derivedFrom":makeQuery(id+"F1.opExtrude","SWEPT_FACE",FACE,{"disambiguationData":[OSD([subQ4])]})}),makeQuery(id+"F21.opExtrude","CAP_FACE",FACE,{"disambiguationData":[OSD([sQuery(id+"F20.wireOp",EDGE,"E27.bottom"),sQuery(id+"F20.wireOp",EDGE,"E27.top"),sQuery(id+"F20.wireOp",EDGE,"E27.left"),sQuery(id+"F20.wireOp",EDGE,"E27.right")])],"isStart":true})]}),makeQuery(id+"F32.opExtrude","SWEPT_FACE",FACE,{"disambiguationData":[OSD([sQuery(id+"F31.wireOp",EDGE,"E38.bottom")])]})]});}
            var sketch = newSketch(context, id + "F39", { "sketchPlane" : qUnion([Q0])});
            skLineSegment(sketch, "E45.bottom", {"start": v(-72.28, 0) * mm, "end": v(-64.83, 0) * mm});
            skLineSegment(sketch, "E45.top", {"start": v(-72.28, -21.03) * mm, "end": v(-64.83, -21.03) * mm});
            skLineSegment(sketch, "E45.left", {"start": v(-72.28, 0) * mm, "end": v(-72.28, -21.03) * mm});
            skLineSegment(sketch, "E45.right", {"start": v(-64.83, 0) * mm, "end": v(-64.83, -21.03) * mm});
            skSolve(sketch);
        }
        {
            var Q0;
            Q0 = qSketchRegion(id + "F39", true);
            extrude(context, id + "F40", {"entities" : qUnion([Q0]), "operationType" : NewBodyOperationType.ADD, "oppositeDirection" : true, "depth" : 5.08 * mm, "offsetDistance" : 25.4 * mm});
        }
        {
            var Q0;
            {var subQ0=sQuery(id+"F0.wireOp",EDGE,"E2");var subQ3=sQuery(id+"F0.wireOp",EDGE,"E1");Q0=makeQuery(id+"F25.boolean.opBoolean","MERGE",FACE,{"derivedFrom":[makeQuery(id+"F19.boolean.opBoolean","MERGE",FACE,{"derivedFrom":[makeQuery(id+"F5.boolean.opBoolean","SPLIT",FACE,{"disambiguationData":[TD([makeQuery(id+"F1.opExtrude","SWEPT_FACE",FACE,{"disambiguationData":[OSD([subQ0])]})])],"derivedFrom":makeQuery(id+"F1.opExtrude","SWEPT_FACE",FACE,{"disambiguationData":[OSD([subQ3])]})}),makeQuery(id+"F19.opExtrude","CAP_FACE",FACE,{"disambiguationData":[OSD([sQuery(id+"F18.wireOp",EDGE,"E26.bottom"),sQuery(id+"F18.wireOp",EDGE,"E26.top"),sQuery(id+"F18.wireOp",EDGE,"E26.left"),sQuery(id+"F18.wireOp",EDGE,"E26.right")])],"isStart":true})]}),makeQuery(id+"F25.opExtrude","SWEPT_FACE",FACE,{"disambiguationData":[OSD([sQuery(id+"F24.wireOp",EDGE,"E30.top")])]})]});}
            var sketch = newSketch(context, id + "F41", { "sketchPlane" : qUnion([Q0])});
            skLineSegment(sketch, "E46.bottom", {"start": v(15.77, -1.5) * mm, "end": v(23.61, -1.5) * mm});
            skLineSegment(sketch, "E46.top", {"start": v(15.77, -20.32) * mm, "end": v(23.61, -20.32) * mm});
            skLineSegment(sketch, "E46.left", {"start": v(15.77, -1.5) * mm, "end": v(15.77, -20.32) * mm});
            skLineSegment(sketch, "E46.right", {"start": v(23.61, -1.5) * mm, "end": v(23.61, -20.32) * mm});
            skSolve(sketch);
        }
        {
            var Q0;
            Q0 = qSketchRegion(id + "F41", true);
            extrude(context, id + "F42", {"entities" : qUnion([Q0]), "operationType" : NewBodyOperationType.ADD, "oppositeDirection" : true, "depth" : 5.08 * mm, "offsetDistance" : 25.4 * mm});
        }
    });
